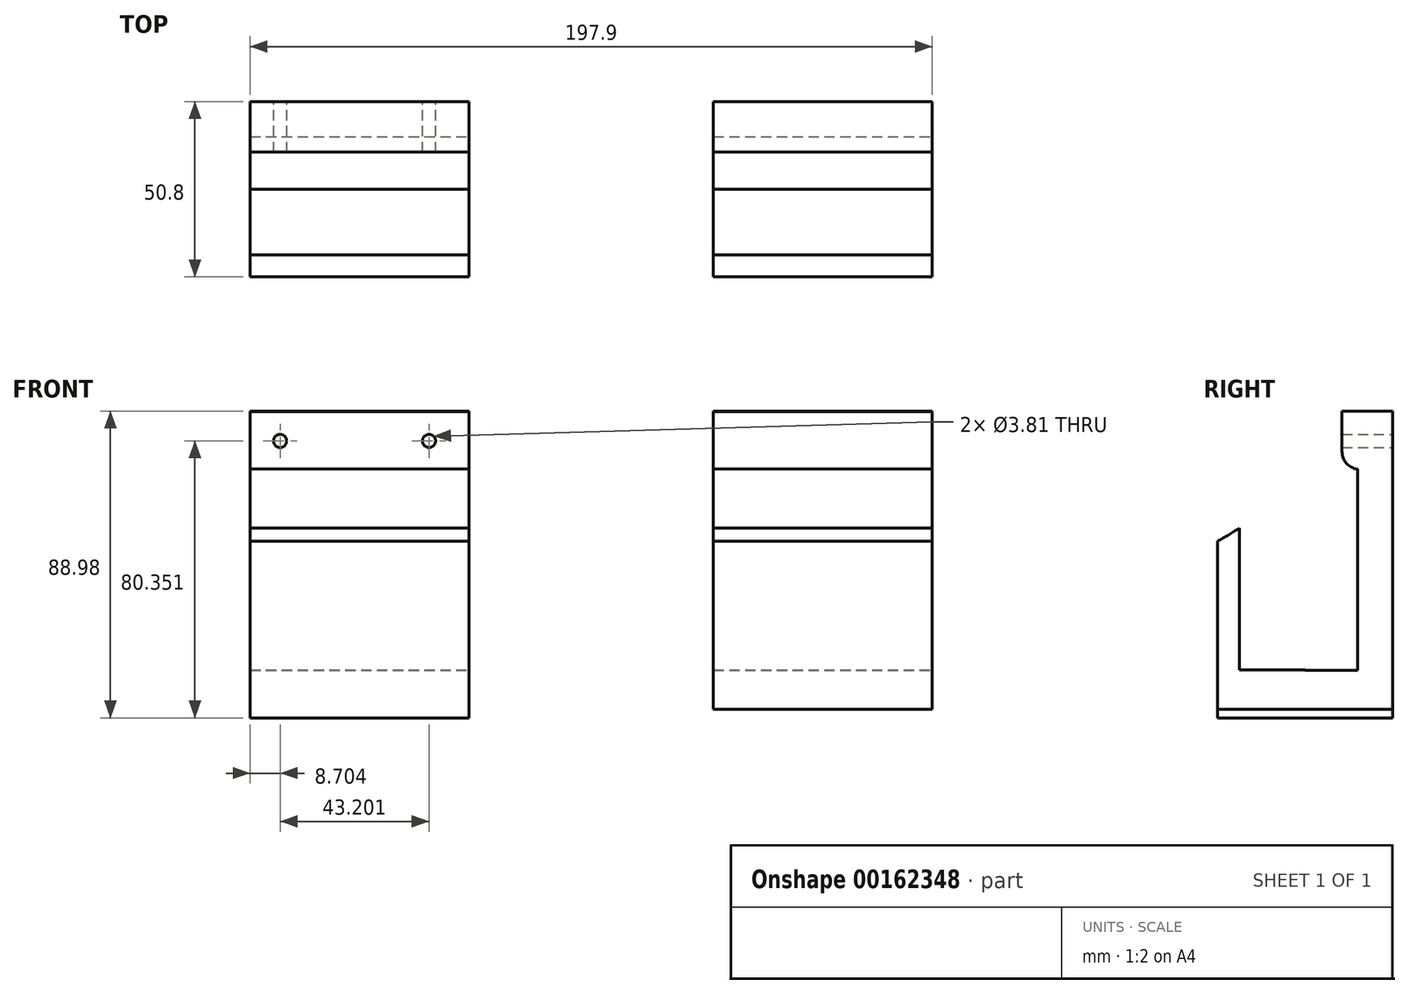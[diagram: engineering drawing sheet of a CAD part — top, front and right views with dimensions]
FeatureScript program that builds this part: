
annotation { "Feature Type Name" : "Feature", "Feature Type Description" : "" }
export const myFeature = defineFeature(function(context is Context, id is Id, definition is map)
    precondition{}
    {
        {
            var Q0;
            Q0=qCreatedBy(makeId("Front.planeOp"),FACE);
            var sketch = newSketch(context, id + "F0", { "sketchPlane" : qUnion([Q0])});
            skLineSegment(sketch, "E0.bottom", {"start": v(-134.4, 131.02) * mm, "end": v(-70.9, 131.02) * mm});
            skLineSegment(sketch, "E0.top", {"start": v(-134.4, -72.18) * mm, "end": v(-70.9, -72.18) * mm});
            skLineSegment(sketch, "E0.left", {"start": v(-134.4, 131.02) * mm, "end": v(-134.4, -72.18) * mm});
            skLineSegment(sketch, "E0.right", {"start": v(-70.9, 131.02) * mm, "end": v(-70.9, -72.18) * mm});
            skLineSegment(sketch, "E1.bottom", {"start": v(0, 133.58) * mm, "end": v(63.5, 133.58) * mm});
            skLineSegment(sketch, "E1.top", {"start": v(0, -69.62) * mm, "end": v(63.5, -69.62) * mm});
            skLineSegment(sketch, "E1.left", {"start": v(0, 133.58) * mm, "end": v(0, -69.62) * mm});
            skLineSegment(sketch, "E1.right", {"start": v(63.5, 133.58) * mm, "end": v(63.5, -69.62) * mm});
            skSolve(sketch);
        }
        {
            var Q0;
            Q0 = qSketchRegion(id + "F0", true);
            extrude(context, id + "F1", {"entities" : qUnion([Q0]), "endBound" : BoundingType.SYMMETRIC, "depth" : 50.8 * mm});
        }
        {
            var Q0;
            Q0=makeQuery(id+"F1.opExtrude","CAP_EDGE",EDGE,{"disambiguationData":[OSD([sQuery(id+"F0.wireOp",EDGE,"E0.bottom")])],"isStart":false});
            var Q1;
            Q1=makeQuery(id+"F1.opExtrude","CAP_EDGE",EDGE,{"disambiguationData":[OSD([sQuery(id+"F0.wireOp",EDGE,"E1.bottom")])],"isStart":false});
            fillet(context, id + "F2", {"entities" : qUnion([Q0, Q1]), "radius" : 5.08 * mm, "tangentPropagation" : true, "allowEdgeOverflow" : false});
        }
        {
            var Q0;
            Q0=qCreatedBy(makeId("Right.planeOp"),FACE);
            var sketch = newSketch(context, id + "F3", { "sketchPlane" : qUnion([Q0])});
            skCircle(sketch, "E2", {"center": v(-66.06, 54.29) * mm, "radius": 85.5 * mm});
            skPoint(sketch, "E2.first.point", {"position": v(0, 0) * mm});
            skPoint(sketch, "E2.second.point", {"position": v(-132.52, 108.09) * mm});
            skPoint(sketch, "E2.third.point", {"position": v(-31.4, 132.45) * mm});
            skSolve(sketch);
        }
        {
            var Q0;
            Q0 = qSketchRegion(id + "F3", true);
            extrude(context, id + "F4", {"entities" : qUnion([Q0]), "operationType" : NewBodyOperationType.REMOVE, "endBound" : BoundingType.SYMMETRIC, "depth" : 304.8 * mm});
        }
        {
            var Q0;
            Q0=qCreatedBy(makeId("Right.planeOp"),FACE);
            var sketch = newSketch(context, id + "F5", { "sketchPlane" : qUnion([Q0])});
            skLineSegment(sketch, "E3.bottom", {"start": v(0, 0) * mm, "end": v(-19.05, 0) * mm});
            skLineSegment(sketch, "E3.top", {"start": v(0, -58.3) * mm, "end": v(-19.05, -58.3) * mm});
            skLineSegment(sketch, "E3.left", {"start": v(0, 0) * mm, "end": v(0, -58.3) * mm});
            skLineSegment(sketch, "E3.right", {"start": v(-19.05, 0) * mm, "end": v(-19.05, -58.3) * mm});
            skSolve(sketch);
        }
        {
            var Q0;
            Q0 = qSketchRegion(id + "F5", true);
            extrude(context, id + "F6", {"entities" : qUnion([Q0]), "operationType" : NewBodyOperationType.REMOVE, "endBound" : BoundingType.SYMMETRIC, "oppositeDirection" : true, "depth" : 381 * mm});
        }
        {
            var Q0;
            Q0=qCreatedBy(makeId("Right.planeOp"),FACE);
            var sketch = newSketch(context, id + "F7", { "sketchPlane" : qUnion([Q0])});
            skLineSegment(sketch, "E4.bottom", {"start": v(0, 0) * mm, "end": v(15.24, 0) * mm});
            skLineSegment(sketch, "E4.top", {"start": v(0, -58.42) * mm, "end": v(15.24, -58.42) * mm});
            skLineSegment(sketch, "E4.left", {"start": v(0, 0) * mm, "end": v(0, -58.42) * mm});
            skLineSegment(sketch, "E4.right", {"start": v(15.24, 0) * mm, "end": v(15.24, -58.42) * mm});
            skSolve(sketch);
        }
        {
            var Q0;
            Q0 = qSketchRegion(id + "F7", true);
            extrude(context, id + "F8", {"entities" : qUnion([Q0]), "operationType" : NewBodyOperationType.REMOVE, "endBound" : BoundingType.SYMMETRIC, "oppositeDirection" : true, "depth" : 381 * mm});
        }
        {
            var Q0;
            {var subQ0=sQuery(id+"F0.wireOp",EDGE,"E0.left");var subQ1=makeQuery(id+"F1.opExtrude","SWEPT_FACE",FACE,{"disambiguationData":[OSD([subQ0])]});var subQ5=sQuery(id+"F5.wireOp",EDGE,"E3.left");Q0=makeQuery(id+"F8.boolean.opBoolean","MERGE",EDGE,{"derivedFrom":[makeQuery(id+"F6.boolean.opBoolean","COPY",EDGE,{"disambiguationData":[TD([subQ1])],"derivedFrom":makeQuery(id+"F6.opExtrude","SWEPT_EDGE",EDGE,{"disambiguationData":[OSD([sQuery(id+"F5.wireOp",EDGE,"E3.bottom"),subQ5])]})}),makeQuery(id+"F8.opExtrude","SWEPT_EDGE",EDGE,{"disambiguationData":[OSD([sQuery(id+"F7.wireOp",EDGE,"E4.bottom"),sQuery(id+"F7.wireOp",EDGE,"E4.left")])]})]});}
            var Q1;
            {var subQ0=sQuery(id+"F0.wireOp",EDGE,"E1.left");var subQ1=makeQuery(id+"F1.opExtrude","SWEPT_FACE",FACE,{"disambiguationData":[OSD([subQ0])]});var subQ5=sQuery(id+"F5.wireOp",EDGE,"E3.left");Q1=makeQuery(id+"F8.boolean.opBoolean","MERGE",EDGE,{"derivedFrom":[makeQuery(id+"F6.boolean.opBoolean","COPY",EDGE,{"disambiguationData":[TD([subQ1])],"derivedFrom":makeQuery(id+"F6.opExtrude","SWEPT_EDGE",EDGE,{"disambiguationData":[OSD([sQuery(id+"F5.wireOp",EDGE,"E3.bottom"),subQ5])]})}),makeQuery(id+"F8.opExtrude","SWEPT_EDGE",EDGE,{"disambiguationData":[OSD([sQuery(id+"F7.wireOp",EDGE,"E4.bottom"),sQuery(id+"F7.wireOp",EDGE,"E4.left")])]})]});}
            fillet(context, id + "F9", {"entities" : qUnion([Q0, Q1]), "radius" : 5.08 * mm, "tangentPropagation" : true, "allowEdgeOverflow" : false});
        }
        {
            var Q0;
            Q0=qCreatedBy(makeId("Right.planeOp"),FACE);
            var sketch = newSketch(context, id + "F10", { "sketchPlane" : qUnion([Q0])});
            skLineSegment(sketch, "E5.bottom", {"start": v(-42.76, 77.35) * mm, "end": v(94.43, 77.35) * mm});
            skLineSegment(sketch, "E5.top", {"start": v(-42.76, 193.17) * mm, "end": v(94.43, 193.17) * mm});
            skLineSegment(sketch, "E5.left", {"start": v(-42.76, 77.35) * mm, "end": v(-42.76, 193.17) * mm});
            skLineSegment(sketch, "E5.right", {"start": v(94.43, 77.35) * mm, "end": v(94.43, 193.17) * mm});
            skPoint(sketch, "E5.middle", {"position": v(25.84, 135.26) * mm});
            skSolve(sketch);
        }
        {
            var Q0;
            Q0 = qSketchRegion(id + "F10", true);
            extrude(context, id + "F11", {"entities" : qUnion([Q0]), "operationType" : NewBodyOperationType.REMOVE, "endBound" : BoundingType.SYMMETRIC, "oppositeDirection" : true, "depth" : 1270 * mm});
        }
        {
            var Q0;
            Q0=qCreatedBy(makeId("Right.planeOp"),FACE);
            var sketch = newSketch(context, id + "F12", { "sketchPlane" : qUnion([Q0])});
            skLineSegment(sketch, "E6.bottom", {"start": v(10.76, -9.45) * mm, "end": v(-2.28, -9.45) * mm});
            skLineSegment(sketch, "E6.top", {"start": v(10.76, 18.92) * mm, "end": v(-2.28, 18.92) * mm});
            skLineSegment(sketch, "E6.left", {"start": v(10.76, -9.45) * mm, "end": v(10.76, 18.92) * mm});
            skLineSegment(sketch, "E6.right", {"start": v(-2.28, -9.45) * mm, "end": v(-2.28, 18.92) * mm});
            skPoint(sketch, "E6.middle", {"position": v(4.24, 4.73) * mm});
            skSolve(sketch);
        }
        {
            var Q0;
            Q0 = qSketchRegion(id + "F12", true);
            extrude(context, id + "F13", {"entities" : qUnion([Q0]), "operationType" : NewBodyOperationType.REMOVE, "endBound" : BoundingType.SYMMETRIC, "oppositeDirection" : true, "depth" : 508 * mm});
        }
        {
            var Q0;
            Q0=qCreatedBy(makeId("Right.planeOp"),FACE);
            var sketch = newSketch(context, id + "F14", { "sketchPlane" : qUnion([Q0])});
            skLineSegment(sketch, "E7.bottom", {"start": v(41.4, 16.8) * mm, "end": v(3.91, 16.8) * mm});
            skLineSegment(sketch, "E7.top", {"start": v(41.4, 97) * mm, "end": v(3.91, 97) * mm});
            skLineSegment(sketch, "E7.left", {"start": v(41.4, 16.8) * mm, "end": v(41.4, 97) * mm});
            skLineSegment(sketch, "E7.right", {"start": v(3.91, 16.8) * mm, "end": v(3.91, 97) * mm});
            skPoint(sketch, "E7.middle", {"position": v(22.66, 56.9) * mm});
            skSolve(sketch);
        }
        {
            var Q0;
            Q0 = qSketchRegion(id + "F14", true);
            extrude(context, id + "F15", {"entities" : qUnion([Q0]), "operationType" : NewBodyOperationType.REMOVE, "endBound" : BoundingType.SYMMETRIC, "oppositeDirection" : true, "depth" : 508 * mm});
        }
        {
            var Q0;
            Q0=qCreatedBy(makeId("Front.planeOp"),FACE);
            var sketch = newSketch(context, id + "F16", { "sketchPlane" : qUnion([Q0])});
            skCircle(sketch, "E8", {"center": v(-125.7, 8.17) * mm, "radius": 1.9 * mm});
            skCircle(sketch, "E9", {"center": v(-82.5, 8.17) * mm, "radius": 1.9 * mm});
            skSolve(sketch);
        }
        {
            var Q0;
            Q0 = qSketchRegion(id + "F16", true);
            extrude(context, id + "F17", {"entities" : qUnion([Q0]), "operationType" : NewBodyOperationType.REMOVE, "endBound" : BoundingType.SYMMETRIC, "depth" : 254 * mm});
        }
        {
            var Q0;
            {var subQ0=sQuery(id+"F0.wireOp",EDGE,"E0.left");var subQ1=makeQuery(id+"F1.opExtrude","SWEPT_FACE",FACE,{"disambiguationData":[OSD([subQ0])]});Q0=makeQuery(id+"F13.boolean.opBoolean","INTERSECT",EDGE,{"derivedFrom":[makeQuery(id+"F8.boolean.opBoolean","COPY",FACE,{"disambiguationData":[TD([subQ1])],"derivedFrom":makeQuery(id+"F8.opExtrude","SWEPT_FACE",FACE,{"disambiguationData":[OSD([sQuery(id+"F7.wireOp",EDGE,"E4.bottom")])]})}),makeQuery(id+"F13.opExtrude","SWEPT_FACE",FACE,{"disambiguationData":[OSD([sQuery(id+"F12.wireOp",EDGE,"E6.left")])]})]});}
            var Q1;
            {var subQ0=sQuery(id+"F0.wireOp",EDGE,"E1.left");var subQ1=makeQuery(id+"F1.opExtrude","SWEPT_FACE",FACE,{"disambiguationData":[OSD([subQ0])]});Q1=makeQuery(id+"F13.boolean.opBoolean","INTERSECT",EDGE,{"derivedFrom":[makeQuery(id+"F8.boolean.opBoolean","COPY",FACE,{"disambiguationData":[TD([subQ1])],"derivedFrom":makeQuery(id+"F8.opExtrude","SWEPT_FACE",FACE,{"disambiguationData":[OSD([sQuery(id+"F7.wireOp",EDGE,"E4.bottom")])]})}),makeQuery(id+"F13.opExtrude","SWEPT_FACE",FACE,{"disambiguationData":[OSD([sQuery(id+"F12.wireOp",EDGE,"E6.left")])]})]});}
            fillet(context, id + "F18", {"entities" : qUnion([Q0, Q1]), "radius" : 5.08 * mm, "tangentPropagation" : true, "allowEdgeOverflow" : false});
        }
    });
